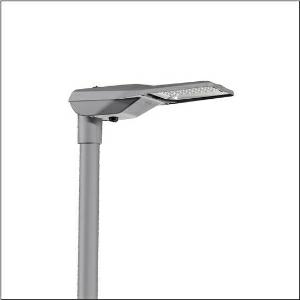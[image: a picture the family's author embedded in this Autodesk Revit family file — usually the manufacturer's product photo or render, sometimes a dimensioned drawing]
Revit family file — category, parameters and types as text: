
# Revit family: streetlight_sl_21_mini___p0_5a_5xe2v33t08hb_c971
name_source: partatom
category: Lighting Fixtures
units: mm (PartAtom-declared; Revit-internal decimal feet)

## family parameters
Cut with Voids When Loaded = No
Host = Face
Light Source = No
Part Type = Normal
Room Calculation Point = No
Round Connector Dimension = Use Diameter
Shared = No

## types (1)
- --- (1 x LED, 8890 lm, 66 W, 3000K)
    Apparent Load = 66 VA
    CIE Flux Codes = 37 73 96 100 100
    Color Rendering = 70
    Color Temperature = 3000K
    Default Elevation = 1800 mm
    Description = Streetlight SL 21 mini, mast luminaire, primary light control with lens, of PMMA, primary optical cover: cover, of toughened safety glass, transparent, light distribution: P0.5a, light emission: direct distribution, primary light characteristic: asymmetric, installation type: post-top, side-entry, LED, High Power LED, rated luminous flux: 8.890lm, luminous efficacy: 135lm/W, light colour: 730, colour temperature: 3000K, control gear: D4i, control: pre-setting: logarithmic dimming characteristic, flexible luminous flux parameterisation, time-dependent luminous flux control, constant luminous flux control, overheat protection, mains connection: 220..240V, AC, 50/60Hz, start of lifetime: 66W, end of service life: 69W, reduction: 30W, luminaire housing, of diecast aluminium, powder-coated, SITECO metallic grey (DB 702S), corrosivity category C5 high according to DIN EN ISO 12944, multi-level sealing system, sealing non-destructively replaceable, inclination adjustable: 0°, 5°, 10°, 15°, please order mast flange separately, length: 628mm, width: 235mm, height: 110mm, mast flange for spigot size: 42mm (side-entry): 5XC10008XM4, 60/48mm (side-entry/post-top): 5XC10108XM2, 76/60mm (side-entry/post-top): 5XC10108XM1, mounting height: 4..8m, Smart Interface below and above, protection rating (complete): IP66, insulation class (complete): insulation class II (safety insulation), certification: CE, ENEC, ENEC+, VDE, impact resistance: IK10, permissible operating ambient temperature for outdoor applications: -40..+50°C, standard-compliant lighting for roads and squares, packaging unit: 1 piece

Light Distribution: P0.5a
    Height = 110 mm
    Lamp = 1 x LED
    Lamp Light Flux = 8890 lm
    Lamp Power = 66 W
    Lamp count = 1
    Length = 625 mm
    Luminous efficacy = 135 lm/W
    Manufacturer = Siteco
    ModVariant = No
    Model = 5XE2V33T08HB
    Number of Poles = 1
    OnlyDefault = Yes
    Power Factor = 1
    Product Name = Streetlight SL 21 mini | P0.5a
    Product group = mast luminaire | pylon top
    ProductGroupID = 6100
    Protection Class = Protection class II
    Protection Degree = IP 66
    RLX_Detail_Level = 1
    RLX_Emergency_Light_Flux = 0 lm
    RLX_Emergency_Type = 0
    RLX_Emergency_Type_DB = No
    RlxData = <blob elided: 91953 chars, md5=5c9ae7d6>
    Socket = socket
    Standby Power = 0 W
    System Light Flux = 8890 lm
    System Power = 66 W
    Type Comments = factory setting: luminous flux: 100 % | dim-lin: 254 | 670 mA
    Type Image = l_1003514.jpg
    URL = http://relux.com
    VarID = @adj_077509
    Voltage = 0 V
    Weight = 0.00 kg
    Width = 234 mm

## geometry (parser evidence)
native form markers: Blend x4, Sweep x10
no freeform markers — native parametric forms only
